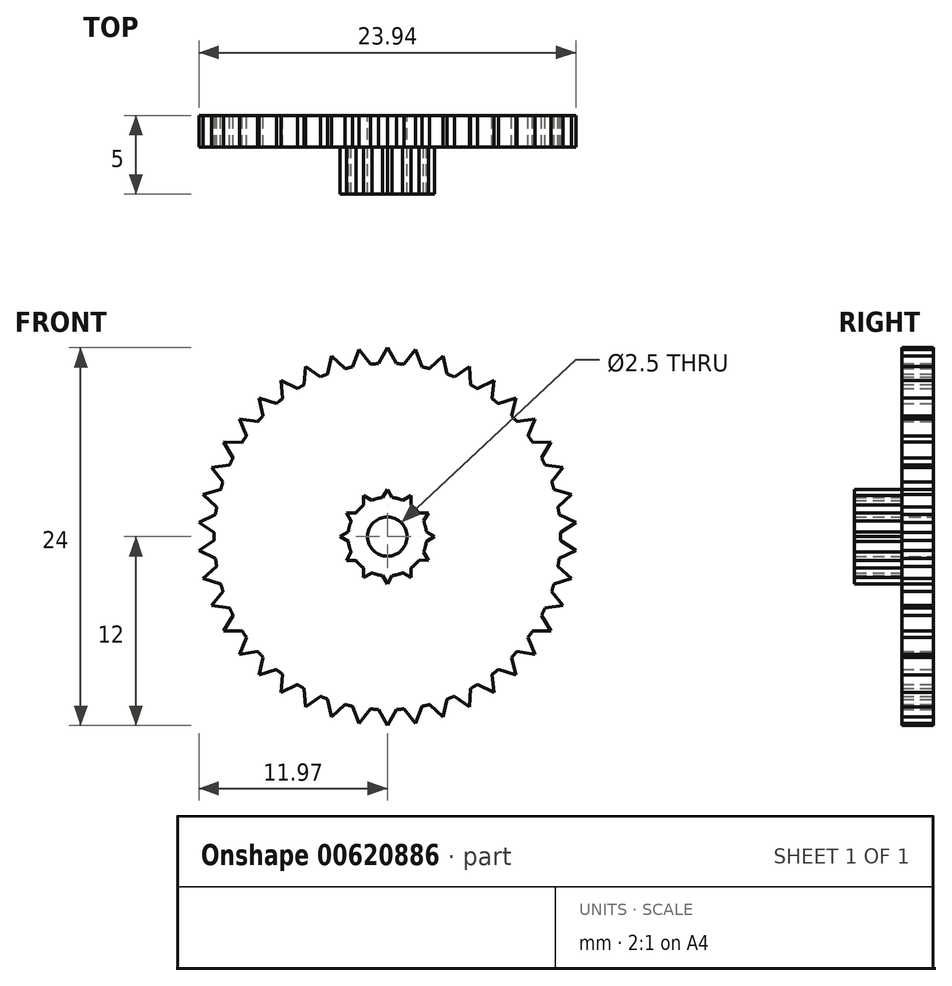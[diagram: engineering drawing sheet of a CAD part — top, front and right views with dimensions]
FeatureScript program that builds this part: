
annotation { "Feature Type Name" : "Feature", "Feature Type Description" : "" }
export const myFeature = defineFeature(function(context is Context, id is Id, definition is map)
    precondition{}
    {
        {
            var Q0;
            Q0=qCreatedBy(makeId("Front.planeOp"),FACE);
            var sketch = newSketch(context, id + "F0", { "sketchPlane" : qUnion([Q0])});
            skCircle(sketch, "E0", {"center": v(0, 0) * mm, "radius": 11 * mm});
            skLineSegment(sketch, "E1", {"start": v(0, 12) * mm, "end": v(-0.57, 10.99) * mm});
            skLineSegment(sketch, "E2.MirrorCS", {"start": v(0, 12) * mm, "end": v(0.57, 10.99) * mm});
            skPoint(sketch, "E3.start.orphan", {"position": v(0, 11) * mm});
            skLineSegment(sketch, "E4.1.0", {"start": v(-1.79, 11.87) * mm, "end": v(-2.2, 10.78) * mm});
            skLineSegment(sketch, "E4.1.1", {"start": v(-1.79, 11.87) * mm, "end": v(-1.07, 10.95) * mm});
            skLineSegment(sketch, "E4.2.0", {"start": v(-3.54, 11.47) * mm, "end": v(-3.78, 10.33) * mm});
            skLineSegment(sketch, "E4.2.1", {"start": v(-3.54, 11.47) * mm, "end": v(-2.7, 10.67) * mm});
            skLineSegment(sketch, "E4.3.0", {"start": v(-5.2, 10.81) * mm, "end": v(-5.28, 9.65) * mm});
            skLineSegment(sketch, "E4.3.1", {"start": v(-5.2, 10.81) * mm, "end": v(-4.25, 10.15) * mm});
            skLineSegment(sketch, "E4.4.0", {"start": v(-6.76, 9.91) * mm, "end": v(-6.66, 8.75) * mm});
            skLineSegment(sketch, "E4.4.1", {"start": v(-6.76, 9.91) * mm, "end": v(-5.72, 9.4) * mm});
            skLineSegment(sketch, "E4.5.0", {"start": v(-8.16, 8.8) * mm, "end": v(-7.9, 7.66) * mm});
            skLineSegment(sketch, "E4.5.1", {"start": v(-8.16, 8.8) * mm, "end": v(-7.05, 8.44) * mm});
            skLineSegment(sketch, "E4.6.0", {"start": v(-9.38, 7.48) * mm, "end": v(-8.94, 6.4) * mm});
            skLineSegment(sketch, "E4.6.1", {"start": v(-9.38, 7.48) * mm, "end": v(-8.23, 7.3) * mm});
            skLineSegment(sketch, "E4.7.0", {"start": v(-10.4, 6) * mm, "end": v(-9.8, 5) * mm});
            skLineSegment(sketch, "E4.7.1", {"start": v(-10.4, 6) * mm, "end": v(-9.23, 5.99) * mm});
            skLineSegment(sketch, "E4.8.0", {"start": v(-11.17, 4.38) * mm, "end": v(-10.43, 3.48) * mm});
            skLineSegment(sketch, "E4.8.1", {"start": v(-11.17, 4.38) * mm, "end": v(-10.02, 4.55) * mm});
            skLineSegment(sketch, "E4.9.0", {"start": v(-11.7, 2.67) * mm, "end": v(-10.84, 1.89) * mm});
            skLineSegment(sketch, "E4.9.1", {"start": v(-11.7, 2.67) * mm, "end": v(-10.58, 3) * mm});
            skLineSegment(sketch, "E4.10.0", {"start": v(-11.97, 0.9) * mm, "end": v(-11, 0.25) * mm});
            skLineSegment(sketch, "E4.10.1", {"start": v(-11.97, 0.9) * mm, "end": v(-10.91, 1.4) * mm});
            skLineSegment(sketch, "E4.11.0", {"start": v(-11.97, -0.9) * mm, "end": v(-10.91, -1.4) * mm});
            skLineSegment(sketch, "E4.11.1", {"start": v(-11.97, -0.9) * mm, "end": v(-11, -0.25) * mm});
            skLineSegment(sketch, "E4.12.0", {"start": v(-11.7, -2.67) * mm, "end": v(-10.58, -3) * mm});
            skLineSegment(sketch, "E4.12.1", {"start": v(-11.7, -2.67) * mm, "end": v(-10.84, -1.89) * mm});
            skLineSegment(sketch, "E4.13.0", {"start": v(-11.17, -4.38) * mm, "end": v(-10.02, -4.55) * mm});
            skLineSegment(sketch, "E4.13.1", {"start": v(-11.17, -4.38) * mm, "end": v(-10.43, -3.48) * mm});
            skLineSegment(sketch, "E4.14.0", {"start": v(-10.4, -6) * mm, "end": v(-9.23, -5.99) * mm});
            skLineSegment(sketch, "E4.14.1", {"start": v(-10.4, -6) * mm, "end": v(-9.8, -5) * mm});
            skLineSegment(sketch, "E4.15.0", {"start": v(-9.38, -7.48) * mm, "end": v(-8.23, -7.3) * mm});
            skLineSegment(sketch, "E4.15.1", {"start": v(-9.38, -7.48) * mm, "end": v(-8.94, -6.4) * mm});
            skLineSegment(sketch, "E4.16.0", {"start": v(-8.16, -8.8) * mm, "end": v(-7.05, -8.44) * mm});
            skLineSegment(sketch, "E4.16.1", {"start": v(-8.16, -8.8) * mm, "end": v(-7.9, -7.66) * mm});
            skLineSegment(sketch, "E4.17.0", {"start": v(-6.76, -9.91) * mm, "end": v(-5.72, -9.4) * mm});
            skLineSegment(sketch, "E4.17.1", {"start": v(-6.76, -9.91) * mm, "end": v(-6.66, -8.75) * mm});
            skLineSegment(sketch, "E4.18.0", {"start": v(-5.2, -10.81) * mm, "end": v(-4.25, -10.15) * mm});
            skLineSegment(sketch, "E4.18.1", {"start": v(-5.2, -10.81) * mm, "end": v(-5.28, -9.65) * mm});
            skLineSegment(sketch, "E4.19.0", {"start": v(-3.54, -11.47) * mm, "end": v(-2.7, -10.67) * mm});
            skLineSegment(sketch, "E4.19.1", {"start": v(-3.54, -11.47) * mm, "end": v(-3.78, -10.33) * mm});
            skLineSegment(sketch, "E4.20.0", {"start": v(-1.79, -11.87) * mm, "end": v(-1.07, -10.95) * mm});
            skLineSegment(sketch, "E4.20.1", {"start": v(-1.79, -11.87) * mm, "end": v(-2.2, -10.78) * mm});
            skLineSegment(sketch, "E4.21.0", {"start": v(0, -12) * mm, "end": v(0.57, -10.99) * mm});
            skLineSegment(sketch, "E4.21.1", {"start": v(0, -12) * mm, "end": v(-0.57, -10.99) * mm});
            skLineSegment(sketch, "E4.22.0", {"start": v(1.79, -11.87) * mm, "end": v(2.2, -10.78) * mm});
            skLineSegment(sketch, "E4.22.1", {"start": v(1.79, -11.87) * mm, "end": v(1.07, -10.95) * mm});
            skLineSegment(sketch, "E4.23.0", {"start": v(3.54, -11.47) * mm, "end": v(3.78, -10.33) * mm});
            skLineSegment(sketch, "E4.23.1", {"start": v(3.54, -11.47) * mm, "end": v(2.7, -10.67) * mm});
            skLineSegment(sketch, "E4.24.0", {"start": v(5.2, -10.81) * mm, "end": v(5.28, -9.65) * mm});
            skLineSegment(sketch, "E4.24.1", {"start": v(5.2, -10.81) * mm, "end": v(4.25, -10.15) * mm});
            skLineSegment(sketch, "E4.25.0", {"start": v(6.76, -9.91) * mm, "end": v(6.66, -8.75) * mm});
            skLineSegment(sketch, "E4.25.1", {"start": v(6.76, -9.91) * mm, "end": v(5.72, -9.4) * mm});
            skLineSegment(sketch, "E4.26.0", {"start": v(8.16, -8.8) * mm, "end": v(7.9, -7.66) * mm});
            skLineSegment(sketch, "E4.26.1", {"start": v(8.16, -8.8) * mm, "end": v(7.05, -8.44) * mm});
            skLineSegment(sketch, "E4.27.0", {"start": v(9.38, -7.48) * mm, "end": v(8.94, -6.4) * mm});
            skLineSegment(sketch, "E4.27.1", {"start": v(9.38, -7.48) * mm, "end": v(8.23, -7.3) * mm});
            skLineSegment(sketch, "E4.28.0", {"start": v(10.4, -6) * mm, "end": v(9.8, -5) * mm});
            skLineSegment(sketch, "E4.28.1", {"start": v(10.4, -6) * mm, "end": v(9.23, -5.99) * mm});
            skLineSegment(sketch, "E4.29.0", {"start": v(11.17, -4.38) * mm, "end": v(10.43, -3.48) * mm});
            skLineSegment(sketch, "E4.29.1", {"start": v(11.17, -4.38) * mm, "end": v(10.02, -4.55) * mm});
            skLineSegment(sketch, "E4.30.0", {"start": v(11.7, -2.67) * mm, "end": v(10.84, -1.89) * mm});
            skLineSegment(sketch, "E4.30.1", {"start": v(11.7, -2.67) * mm, "end": v(10.58, -3) * mm});
            skLineSegment(sketch, "E4.31.0", {"start": v(11.97, -0.9) * mm, "end": v(11, -0.25) * mm});
            skLineSegment(sketch, "E4.31.1", {"start": v(11.97, -0.9) * mm, "end": v(10.91, -1.4) * mm});
            skLineSegment(sketch, "E4.32.0", {"start": v(11.97, 0.9) * mm, "end": v(10.91, 1.4) * mm});
            skLineSegment(sketch, "E4.32.1", {"start": v(11.97, 0.9) * mm, "end": v(11, 0.25) * mm});
            skLineSegment(sketch, "E4.33.0", {"start": v(11.7, 2.67) * mm, "end": v(10.58, 3) * mm});
            skLineSegment(sketch, "E4.33.1", {"start": v(11.7, 2.67) * mm, "end": v(10.84, 1.89) * mm});
            skLineSegment(sketch, "E4.34.0", {"start": v(11.17, 4.38) * mm, "end": v(10.02, 4.55) * mm});
            skLineSegment(sketch, "E4.34.1", {"start": v(11.17, 4.38) * mm, "end": v(10.43, 3.48) * mm});
            skLineSegment(sketch, "E4.35.0", {"start": v(10.4, 6) * mm, "end": v(9.23, 5.99) * mm});
            skLineSegment(sketch, "E4.35.1", {"start": v(10.4, 6) * mm, "end": v(9.8, 5) * mm});
            skLineSegment(sketch, "E4.36.0", {"start": v(9.38, 7.48) * mm, "end": v(8.23, 7.3) * mm});
            skLineSegment(sketch, "E4.36.1", {"start": v(9.38, 7.48) * mm, "end": v(8.94, 6.4) * mm});
            skLineSegment(sketch, "E4.37.0", {"start": v(8.16, 8.8) * mm, "end": v(7.05, 8.44) * mm});
            skLineSegment(sketch, "E4.37.1", {"start": v(8.16, 8.8) * mm, "end": v(7.9, 7.66) * mm});
            skLineSegment(sketch, "E4.38.0", {"start": v(6.76, 9.91) * mm, "end": v(5.72, 9.4) * mm});
            skLineSegment(sketch, "E4.38.1", {"start": v(6.76, 9.91) * mm, "end": v(6.66, 8.75) * mm});
            skLineSegment(sketch, "E4.39.0", {"start": v(5.2, 10.81) * mm, "end": v(4.25, 10.15) * mm});
            skLineSegment(sketch, "E4.39.1", {"start": v(5.2, 10.81) * mm, "end": v(5.28, 9.65) * mm});
            skLineSegment(sketch, "E4.40.0", {"start": v(3.54, 11.47) * mm, "end": v(2.7, 10.67) * mm});
            skLineSegment(sketch, "E4.40.1", {"start": v(3.54, 11.47) * mm, "end": v(3.78, 10.33) * mm});
            skLineSegment(sketch, "E4.41.0", {"start": v(1.79, 11.87) * mm, "end": v(1.07, 10.95) * mm});
            skLineSegment(sketch, "E4.41.1", {"start": v(1.79, 11.87) * mm, "end": v(2.2, 10.78) * mm});
            skCircle(sketch, "E5", {"center": v(0, 0) * mm, "radius": 2.5 * mm});
            skLineSegment(sketch, "E6", {"start": v(0, 2.5) * mm, "end": v(0, 3) * mm});
            skLineSegment(sketch, "E7", {"start": v(0, 3) * mm, "end": v(-0.3, 2.48) * mm});
            skLineSegment(sketch, "E8.MirrorCS", {"start": v(0, 3) * mm, "end": v(0.3, 2.48) * mm});
            skLineSegment(sketch, "E9.1.0", {"start": v(1.5, 2.6) * mm, "end": v(1.5, 2) * mm});
            skLineSegment(sketch, "E9.1.1", {"start": v(1.5, 2.6) * mm, "end": v(0.98, 2.3) * mm});
            skLineSegment(sketch, "E9.2.0", {"start": v(2.6, 1.5) * mm, "end": v(2.3, 0.98) * mm});
            skLineSegment(sketch, "E9.2.1", {"start": v(2.6, 1.5) * mm, "end": v(2, 1.5) * mm});
            skLineSegment(sketch, "E9.3.0", {"start": v(3, 0) * mm, "end": v(2.48, -0.3) * mm});
            skLineSegment(sketch, "E9.3.1", {"start": v(3, 0) * mm, "end": v(2.48, 0.3) * mm});
            skLineSegment(sketch, "E9.4.0", {"start": v(2.6, -1.5) * mm, "end": v(2, -1.5) * mm});
            skLineSegment(sketch, "E9.4.1", {"start": v(2.6, -1.5) * mm, "end": v(2.3, -0.98) * mm});
            skLineSegment(sketch, "E9.5.0", {"start": v(1.5, -2.6) * mm, "end": v(0.98, -2.3) * mm});
            skLineSegment(sketch, "E9.5.1", {"start": v(1.5, -2.6) * mm, "end": v(1.5, -2) * mm});
            skLineSegment(sketch, "E9.6.0", {"start": v(0, -3) * mm, "end": v(-0.3, -2.48) * mm});
            skLineSegment(sketch, "E9.6.1", {"start": v(0, -3) * mm, "end": v(0.3, -2.48) * mm});
            skLineSegment(sketch, "E9.7.0", {"start": v(-1.5, -2.6) * mm, "end": v(-1.5, -2) * mm});
            skLineSegment(sketch, "E9.7.1", {"start": v(-1.5, -2.6) * mm, "end": v(-0.98, -2.3) * mm});
            skLineSegment(sketch, "E9.8.0", {"start": v(-2.6, -1.5) * mm, "end": v(-2.3, -0.98) * mm});
            skLineSegment(sketch, "E9.8.1", {"start": v(-2.6, -1.5) * mm, "end": v(-2, -1.5) * mm});
            skLineSegment(sketch, "E9.9.0", {"start": v(-3, 0) * mm, "end": v(-2.48, 0.3) * mm});
            skLineSegment(sketch, "E9.9.1", {"start": v(-3, 0) * mm, "end": v(-2.48, -0.3) * mm});
            skLineSegment(sketch, "E9.10.0", {"start": v(-2.6, 1.5) * mm, "end": v(-2, 1.5) * mm});
            skLineSegment(sketch, "E9.10.1", {"start": v(-2.6, 1.5) * mm, "end": v(-2.3, 0.98) * mm});
            skLineSegment(sketch, "E9.11.0", {"start": v(-1.5, 2.6) * mm, "end": v(-0.98, 2.3) * mm});
            skLineSegment(sketch, "E9.11.1", {"start": v(-1.5, 2.6) * mm, "end": v(-1.5, 2) * mm});
            skLineSegment(sketch, "E9.anchor1", {"start": v(0, 0) * mm, "end": v(0.3, 2.48) * mm, "construction": true});
            skLineSegment(sketch, "E9.anchor2", {"start": v(0, 0) * mm, "end": v(-0.98, 2.3) * mm, "construction": true});
            skSolve(sketch);
        }
        {
            var Q0;
            Q0 = qSketchRegion(id + "F0", true);
            extrude(context, id + "F1", {"entities" : qUnion([Q0]), "depth" : 2 * mm, "offsetDistance" : 25 * mm});
        }
        {
            var Q0;
            Q0=qCreatedBy(makeId("Front.planeOp"),FACE);
            var sketch = newSketch(context, id + "F2", { "sketchPlane" : qUnion([Q0])});
            skCircle(sketch, "E10", {"center": v(0, 0) * mm, "radius": 2.5 * mm});
            skLineSegment(sketch, "E11", {"start": v(0, 2.5) * mm, "end": v(0, 3) * mm});
            skLineSegment(sketch, "E12", {"start": v(0, 3) * mm, "end": v(-0.3, 2.48) * mm});
            skLineSegment(sketch, "E13", {"start": v(-0.3, 2.48) * mm, "end": v(0, 3) * mm});
            skLineSegment(sketch, "E14", {"start": v(0, 3) * mm, "end": v(0.3, 2.48) * mm});
            skLineSegment(sketch, "E15.1.0", {"start": v(0.98, 2.3) * mm, "end": v(1.5, 2.6) * mm});
            skLineSegment(sketch, "E15.1.1", {"start": v(1.5, 2.6) * mm, "end": v(1.5, 2) * mm});
            skLineSegment(sketch, "E15.2.0", {"start": v(2, 1.5) * mm, "end": v(2.6, 1.5) * mm});
            skLineSegment(sketch, "E15.2.1", {"start": v(2.6, 1.5) * mm, "end": v(2.3, 0.98) * mm});
            skLineSegment(sketch, "E15.3.0", {"start": v(2.48, 0.3) * mm, "end": v(3, 0) * mm});
            skLineSegment(sketch, "E15.3.1", {"start": v(3, 0) * mm, "end": v(2.48, -0.3) * mm});
            skLineSegment(sketch, "E15.4.0", {"start": v(2.3, -0.98) * mm, "end": v(2.6, -1.5) * mm});
            skLineSegment(sketch, "E15.4.1", {"start": v(2.6, -1.5) * mm, "end": v(2, -1.5) * mm});
            skLineSegment(sketch, "E15.5.0", {"start": v(1.5, -2) * mm, "end": v(1.5, -2.6) * mm});
            skLineSegment(sketch, "E15.5.1", {"start": v(1.5, -2.6) * mm, "end": v(0.98, -2.3) * mm});
            skLineSegment(sketch, "E15.6.0", {"start": v(0.3, -2.48) * mm, "end": v(0, -3) * mm});
            skLineSegment(sketch, "E15.6.1", {"start": v(0, -3) * mm, "end": v(-0.3, -2.48) * mm});
            skLineSegment(sketch, "E15.7.0", {"start": v(-0.98, -2.3) * mm, "end": v(-1.5, -2.6) * mm});
            skLineSegment(sketch, "E15.7.1", {"start": v(-1.5, -2.6) * mm, "end": v(-1.5, -2) * mm});
            skLineSegment(sketch, "E15.8.0", {"start": v(-2, -1.5) * mm, "end": v(-2.6, -1.5) * mm});
            skLineSegment(sketch, "E15.8.1", {"start": v(-2.6, -1.5) * mm, "end": v(-2.3, -0.98) * mm});
            skLineSegment(sketch, "E15.9.0", {"start": v(-2.48, -0.3) * mm, "end": v(-3, 0) * mm});
            skLineSegment(sketch, "E15.9.1", {"start": v(-3, 0) * mm, "end": v(-2.48, 0.3) * mm});
            skLineSegment(sketch, "E15.10.0", {"start": v(-2.3, 0.98) * mm, "end": v(-2.6, 1.5) * mm});
            skLineSegment(sketch, "E15.10.1", {"start": v(-2.6, 1.5) * mm, "end": v(-2, 1.5) * mm});
            skLineSegment(sketch, "E15.11.0", {"start": v(-1.5, 2) * mm, "end": v(-1.5, 2.6) * mm});
            skLineSegment(sketch, "E15.11.1", {"start": v(-1.5, 2.6) * mm, "end": v(-0.98, 2.3) * mm});
            skLineSegment(sketch, "E15.anchor1", {"start": v(0, 0) * mm, "end": v(-0.3, 2.48) * mm, "construction": true});
            skLineSegment(sketch, "E15.anchor2", {"start": v(0, 0) * mm, "end": v(-1.5, 2) * mm, "construction": true});
            skSolve(sketch);
        }
        {
            var Q0;
            Q0 = qSketchRegion(id + "F2", true);
            extrude(context, id + "F3", {"entities" : qUnion([Q0]), "operationType" : NewBodyOperationType.ADD, "depth" : 5 * mm, "offsetDistance" : 25 * mm});
        }
        {
            var Q0;
            Q0=qCreatedBy(makeId("Front.planeOp"),FACE);
            var sketch = newSketch(context, id + "F4", { "sketchPlane" : qUnion([Q0])});
            skCircle(sketch, "E16", {"center": v(0, 0) * mm, "radius": 1.25 * mm});
            skSolve(sketch);
        }
        {
            var Q0;
            Q0 = qSketchRegion(id + "F4", true);
            extrude(context, id + "F5", {"entities" : qUnion([Q0]), "operationType" : NewBodyOperationType.REMOVE, "depth" : 25 * mm, "offsetDistance" : 25 * mm});
        }
    });
